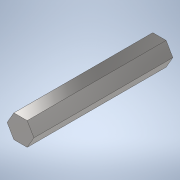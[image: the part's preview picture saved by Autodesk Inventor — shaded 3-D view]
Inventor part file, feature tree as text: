
AUTODESK INVENTOR PART (.ipt)
format: ipt  version: 2020 (Build 240168000, 168)  size: 99,328 bytes
history: native  units: in
note: dims shown in document units (in); Inventor stores cm internally (conversion verified against a paired STEP export)
features: extrude x1, sketch x1
ambient origin geometry x8: Origin, YZ Plane, XZ Plane, XY Plane, X Axis, Y Axis, Z Axis, Center Point
bodies: Solid1 (feature_tree)
feature tree (2):
  extrude  "Extrusion1"  Depth=3.0in TaperAngle=0.0deg
  sketch  "Sketch1"  dims[d0=0.5in d1=3.0in d2=0.0in]
